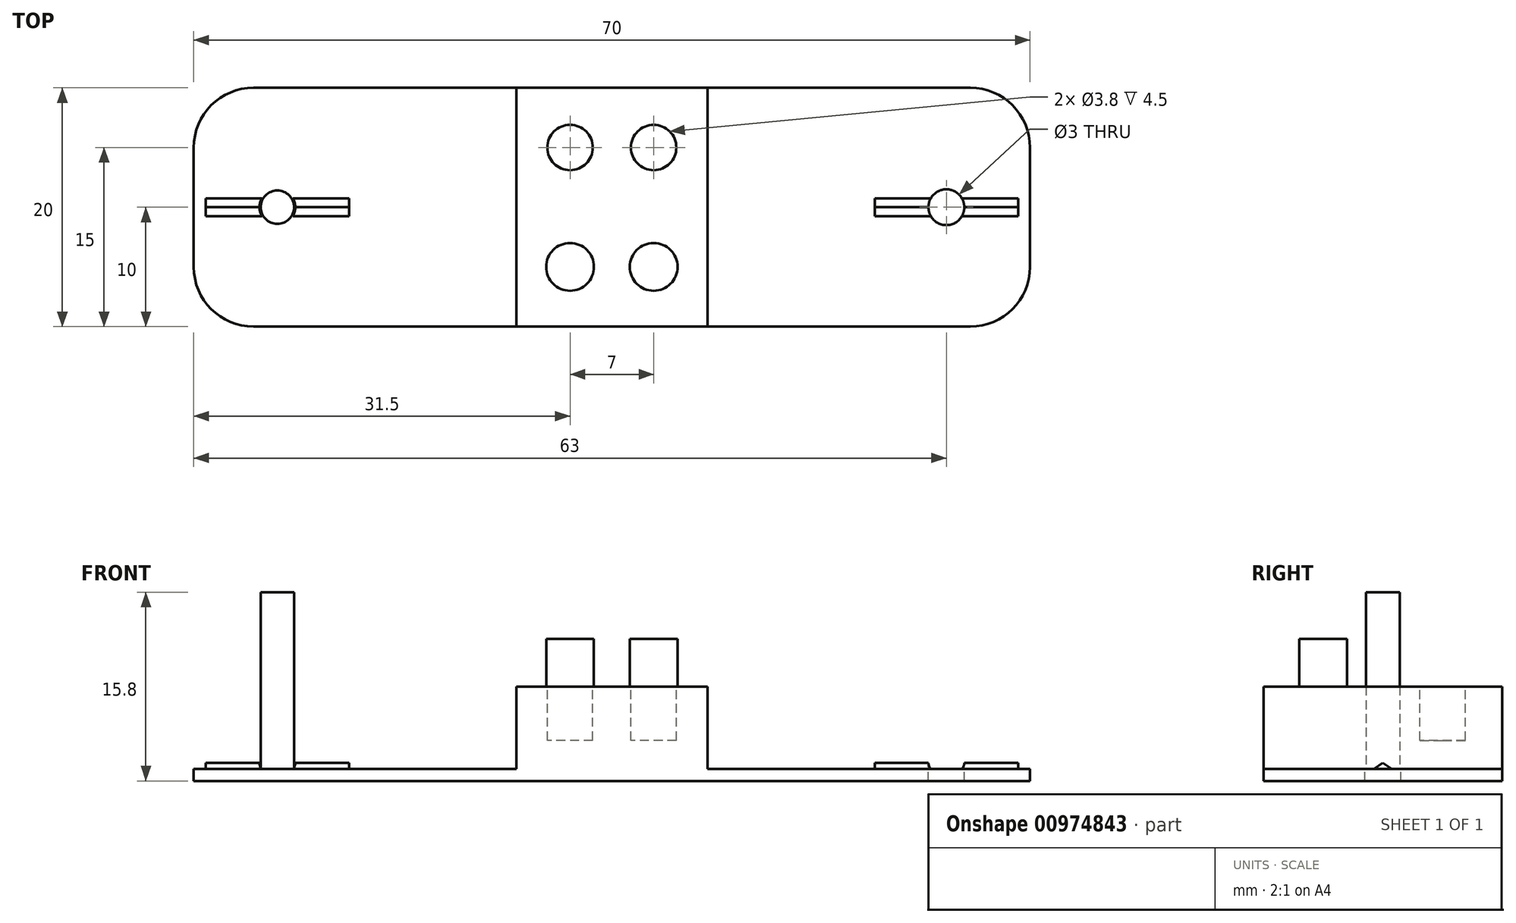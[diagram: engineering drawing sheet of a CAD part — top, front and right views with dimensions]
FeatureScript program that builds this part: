
annotation { "Feature Type Name" : "Feature", "Feature Type Description" : "" }
export const myFeature = defineFeature(function(context is Context, id is Id, definition is map)
    precondition{}
    {
        {
            var Q0;
            Q0=qCreatedBy(makeId("Top.planeOp"),FACE);
            var sketch = newSketch(context, id + "F0", { "sketchPlane" : qUnion([Q0])});
            skLineSegment(sketch, "E0.bottom", {"start": v(35, 10) * mm, "end": v(-35, 10) * mm});
            skLineSegment(sketch, "E0.top", {"start": v(35, -10) * mm, "end": v(-35, -10) * mm});
            skLineSegment(sketch, "E0.left", {"start": v(35, 10) * mm, "end": v(35, -10) * mm});
            skLineSegment(sketch, "E0.right", {"start": v(-35, 10) * mm, "end": v(-35, -10) * mm});
            skSolve(sketch);
        }
        {
            var Q0;
            Q0=qSketchRegion(id+"F0",true);
            extrude(context, id + "F1", {"entities" : qUnion([Q0]), "depth" : 1 * mm, "offsetDistance" : 25 * mm});
        }
        {
            var Q0;
            Q0=makeQuery(id+"F1.opExtrude","CAP_FACE",FACE,{"disambiguationData":[OSD([sQuery(id+"F0.wireOp",EDGE,"E0.bottom"),sQuery(id+"F0.wireOp",EDGE,"E0.top"),sQuery(id+"F0.wireOp",EDGE,"E0.left"),sQuery(id+"F0.wireOp",EDGE,"E0.right")])],"isStart":false});
            var sketch = newSketch(context, id + "F2", { "sketchPlane" : qUnion([Q0])});
            skCircle(sketch, "E1", {"center": v(-28, 0) * mm, "radius": 1.5 * mm});
            skPoint(sketch, "E1.centerSnap0", {"position": v(-35, 0) * mm});
            skCircle(sketch, "E2", {"center": v(28, 0) * mm, "radius": 1.5 * mm});
            skPoint(sketch, "E2.centerSnap0", {"position": v(35, 0) * mm});
            skSolve(sketch);
        }
        {
            var Q0;
            Q0=sQuery(id+"F2.wireOp",VERTEX,"E1.center");
            var Q1;
            Q1=sQuery(id+"F2.wireOp",VERTEX,"E2.center");
            var Q2;
            Q2=makeQuery(id+"F1.opExtrude","SWEPT_BODY",BODY,{"disambiguationData":[OSD([sQuery(id+"F0.wireOp",EDGE,"E0.bottom"),sQuery(id+"F0.wireOp",EDGE,"E0.top"),sQuery(id+"F0.wireOp",EDGE,"E0.left"),sQuery(id+"F0.wireOp",EDGE,"E0.right")])]});
            hole(context, id + "F3", {"style" : HoleStyle.SIMPLE, "endStyle" : HoleEndStyle.THROUGH, "holeDiameter" : 3 * mm, "majorDiameter" : 5 * mm, "isTappedThrough" : true, "tappedDepth" : 12 * mm, "tapClearance" : 3, "locations" : qUnion([Q0, Q1]), "scope" : qUnion([Q2])});
        }
        {
            var Q0;
            Q0=makeQuery(id+"F1.opExtrude","SWEPT_EDGE",EDGE,{"disambiguationData":[OSD([sQuery(id+"F0.wireOp",EDGE,"E0.bottom"),sQuery(id+"F0.wireOp",EDGE,"E0.right")])]});
            var Q1;
            Q1=makeQuery(id+"F1.opExtrude","SWEPT_EDGE",EDGE,{"disambiguationData":[OSD([sQuery(id+"F0.wireOp",EDGE,"E0.top"),sQuery(id+"F0.wireOp",EDGE,"E0.right")])]});
            var Q2;
            Q2=makeQuery(id+"F1.opExtrude","SWEPT_EDGE",EDGE,{"disambiguationData":[OSD([sQuery(id+"F0.wireOp",EDGE,"E0.bottom"),sQuery(id+"F0.wireOp",EDGE,"E0.left")])]});
            var Q3;
            Q3=makeQuery(id+"F1.opExtrude","SWEPT_EDGE",EDGE,{"disambiguationData":[OSD([sQuery(id+"F0.wireOp",EDGE,"E0.top"),sQuery(id+"F0.wireOp",EDGE,"E0.left")])]});
            fillet(context, id + "F4", {"entities" : qUnion([Q0, Q1, Q2, Q3]), "radius" : 5 * mm, "tangentPropagation" : true, "allowEdgeOverflow" : false});
        }
        {
            var Q0;
            Q0=makeQuery(id+"F1.opExtrude","CAP_FACE",FACE,{"disambiguationData":[OSD([sQuery(id+"F0.wireOp",EDGE,"E0.bottom"),sQuery(id+"F0.wireOp",EDGE,"E0.top"),sQuery(id+"F0.wireOp",EDGE,"E0.left"),sQuery(id+"F0.wireOp",EDGE,"E0.right")])],"isStart":false});
            var sketch = newSketch(context, id + "F5", { "sketchPlane" : qUnion([Q0])});
            skLineSegment(sketch, "E3", {"start": v(-34, 0.75) * mm, "end": v(-29.3, 0.75) * mm});
            skLineSegment(sketch, "E4", {"start": v(-22, 0.75) * mm, "end": v(-22, -0.75) * mm});
            skLineSegment(sketch, "E5", {"start": v(-22, -0.75) * mm, "end": v(-26.7, -0.75) * mm});
            skLineSegment(sketch, "E6", {"start": v(-34, -0.75) * mm, "end": v(-34, 0.75) * mm});
            skArc(sketch, "E7", {"start": v(-29.3, 0.75) * mm, "mid": v(-29.5, 0) * mm, "end": v(-29.3, -0.75) * mm});
            skLineSegment(sketch, "E8.trimOffspring", {"start": v(-26.7, 0.75) * mm, "end": v(-22, 0.75) * mm});
            skLineSegment(sketch, "E9.trimOffspring", {"start": v(-29.3, -0.75) * mm, "end": v(-34, -0.75) * mm});
            skArc(sketch, "E10.trimOffspring", {"start": v(-26.7, -0.75) * mm, "mid": v(-26.5, 0) * mm, "end": v(-26.7, 0.75) * mm});
            skSolve(sketch);
        }
        {
            var Q0;
            Q0=makeQuery(id+"F1.opExtrude","CAP_FACE",FACE,{"disambiguationData":[OSD([sQuery(id+"F0.wireOp",EDGE,"E0.bottom"),sQuery(id+"F0.wireOp",EDGE,"E0.top"),sQuery(id+"F0.wireOp",EDGE,"E0.left"),sQuery(id+"F0.wireOp",EDGE,"E0.right")])],"isStart":false});
            var sketch = newSketch(context, id + "F6", { "sketchPlane" : qUnion([Q0])});
            skLineSegment(sketch, "E11", {"start": v(22, 0.75) * mm, "end": v(26.7, 0.75) * mm});
            skLineSegment(sketch, "E12", {"start": v(34, 0.75) * mm, "end": v(34, -0.75) * mm});
            skLineSegment(sketch, "E13", {"start": v(34, -0.75) * mm, "end": v(29.3, -0.75) * mm});
            skLineSegment(sketch, "E14", {"start": v(22, -0.75) * mm, "end": v(22, 0.75) * mm});
            skArc(sketch, "E15", {"start": v(26.7, 0.75) * mm, "mid": v(26.5, 0) * mm, "end": v(26.7, -0.75) * mm});
            skLineSegment(sketch, "E16.trimOffspring", {"start": v(29.3, 0.75) * mm, "end": v(34, 0.75) * mm});
            skLineSegment(sketch, "E17.trimOffspring", {"start": v(26.7, -0.75) * mm, "end": v(22, -0.75) * mm});
            skArc(sketch, "E18.trimOffspring", {"start": v(29.3, -0.75) * mm, "mid": v(29.5, 0) * mm, "end": v(29.3, 0.75) * mm});
            skSolve(sketch);
        }
        {
            var Q0;
            Q0=makeQuery(id+"F5.imprint","IMPRINT",FACE,{"disambiguationData":[TD([[makeQuery(id+"F5.imprint","IMPRINT",EDGE,{"derivedFrom":sQuery(id+"F5.wireOp",EDGE,"E3")}),-1.0]])]});
            var Q1;
            Q1=makeQuery(id+"F5.imprint","IMPRINT",FACE,{"disambiguationData":[TD([[makeQuery(id+"F5.imprint","IMPRINT",EDGE,{"derivedFrom":sQuery(id+"F5.wireOp",EDGE,"E4")}),-1.0]])]});
            var Q2;
            Q2=makeQuery(id+"F6.imprint","IMPRINT",FACE,{"disambiguationData":[TD([[makeQuery(id+"F6.imprint","IMPRINT",EDGE,{"derivedFrom":sQuery(id+"F6.wireOp",EDGE,"E11")}),-1.0]])]});
            var Q3;
            Q3=makeQuery(id+"F6.imprint","IMPRINT",FACE,{"disambiguationData":[TD([[makeQuery(id+"F6.imprint","IMPRINT",EDGE,{"derivedFrom":sQuery(id+"F6.wireOp",EDGE,"E12")}),-1.0]])]});
            extrude(context, id + "F7", {"entities" : qUnion([Q0, Q1, Q2, Q3]), "operationType" : NewBodyOperationType.ADD, "depth" : 0.5 * mm, "offsetDistance" : 25 * mm});
        }
        {
            var Q0;
            Q0=makeQuery(id+"F7.opExtrude","SWEPT_FACE",FACE,{"disambiguationData":[OSD([sQuery(id+"F5.wireOp",EDGE,"E6")])]});
            var sketch = newSketch(context, id + "F8", { "sketchPlane" : qUnion([Q0])});
            skLineSegment(sketch, "E19", {"start": v(-0.75, 1) * mm, "end": v(0, 1.5) * mm});
            skLineSegment(sketch, "E20", {"start": v(0, 1.5) * mm, "end": v(0.75, 1) * mm});
            skLineSegment(sketch, "E21", {"start": v(0.75, 1) * mm, "end": v(-0.75, 1) * mm});
            skSolve(sketch);
        }
        {
            var Q0;
            {var subQ0=sQuery(id+"F8.wireOp",EDGE,"E19");Q0=makeQuery(id+"F8.imprint","IMPRINT",FACE,{"disambiguationData":[TD([[makeQuery(id+"F8.imprint","IMPRINT",EDGE,{"derivedFrom":subQ0}),1.0]])]});}
            var Q1;
            {var subQ0=sQuery(id+"F8.wireOp",EDGE,"E20");Q1=makeQuery(id+"F8.imprint","IMPRINT",FACE,{"disambiguationData":[TD([[makeQuery(id+"F8.imprint","IMPRINT",EDGE,{"derivedFrom":subQ0}),1.0]])]});}
            extrude(context, id + "F9", {"entities" : qUnion([Q0, Q1]), "operationType" : NewBodyOperationType.REMOVE, "endBound" : BoundingType.THROUGH_ALL, "oppositeDirection" : true, "depth" : 25 * mm, "offsetDistance" : 25 * mm});
        }
        {
            var Q0;
            Q0=makeQuery(id+"F1.opExtrude","CAP_FACE",FACE,{"disambiguationData":[OSD([sQuery(id+"F0.wireOp",EDGE,"E0.bottom"),sQuery(id+"F0.wireOp",EDGE,"E0.top"),sQuery(id+"F0.wireOp",EDGE,"E0.left"),sQuery(id+"F0.wireOp",EDGE,"E0.right")])],"isStart":false});
            var sketch = newSketch(context, id + "F10", { "sketchPlane" : qUnion([Q0])});
            skLineSegment(sketch, "E22.bottom", {"start": v(-8, -10) * mm, "end": v(8, -10) * mm});
            skLineSegment(sketch, "E22.top", {"start": v(-8, 10) * mm, "end": v(8, 10) * mm});
            skLineSegment(sketch, "E22.left", {"start": v(-8, -10) * mm, "end": v(-8, 10) * mm});
            skLineSegment(sketch, "E22.right", {"start": v(8, -10) * mm, "end": v(8, 10) * mm});
            skPoint(sketch, "E22.middle", {"position": v(0, 0) * mm});
            skSolve(sketch);
        }
        {
            var Q0;
            Q0=makeQuery(id+"F10.imprint","IMPRINT",FACE,{"disambiguationData":[TD([[makeQuery(id+"F10.imprint","IMPRINT",EDGE,{"derivedFrom":sQuery(id+"F10.wireOp",EDGE,"E22.bottom")}),-1.0]])]});
            extrude(context, id + "F11", {"entities" : qUnion([Q0]), "operationType" : NewBodyOperationType.ADD, "depth" : 6.9 * mm, "offsetDistance" : 25 * mm});
        }
        {
            var Q0;
            Q0=makeQuery(id+"F11.opExtrude","CAP_FACE",FACE,{"disambiguationData":[OSD([sQuery(id+"F10.wireOp",EDGE,"E22.bottom"),sQuery(id+"F10.wireOp",EDGE,"E22.top"),sQuery(id+"F10.wireOp",EDGE,"E22.left"),sQuery(id+"F10.wireOp",EDGE,"E22.right")])],"isStart":false});
            var sketch = newSketch(context, id + "F12", { "sketchPlane" : qUnion([Q0])});
            skCircle(sketch, "E23", {"center": v(-3.5, 5) * mm, "radius": 1.9 * mm});
            skCircle(sketch, "E24", {"center": v(3.5, 5) * mm, "radius": 1.9 * mm});
            skCircle(sketch, "E25", {"center": v(-3.5, -5) * mm, "radius": 2 * mm});
            skCircle(sketch, "E26", {"center": v(3.5, -5) * mm, "radius": 2 * mm});
            skSolve(sketch);
        }
        {
            var Q0;
            Q0=makeQuery(id+"F12.imprint","IMPRINT",FACE,{"disambiguationData":[TD([[makeQuery(id+"F12.imprint","IMPRINT",EDGE,{"derivedFrom":sQuery(id+"F12.wireOp",EDGE,"E23")}),1.0]])]});
            var Q1;
            Q1=makeQuery(id+"F12.imprint","IMPRINT",FACE,{"disambiguationData":[TD([[makeQuery(id+"F12.imprint","IMPRINT",EDGE,{"derivedFrom":sQuery(id+"F12.wireOp",EDGE,"E24")}),1.0]])]});
            extrude(context, id + "F13", {"entities" : qUnion([Q0, Q1]), "operationType" : NewBodyOperationType.REMOVE, "oppositeDirection" : true, "depth" : 4.5 * mm, "offsetDistance" : 25 * mm});
        }
        {
            var Q0;
            Q0=makeQuery(id+"F11.opExtrude","CAP_FACE",FACE,{"disambiguationData":[OSD([sQuery(id+"F10.wireOp",EDGE,"E22.bottom"),sQuery(id+"F10.wireOp",EDGE,"E22.top"),sQuery(id+"F10.wireOp",EDGE,"E22.left"),sQuery(id+"F10.wireOp",EDGE,"E22.right")])],"isStart":false});
            var sketch = newSketch(context, id + "F14", { "sketchPlane" : qUnion([Q0])});
            skCircle(sketch, "E27", {"center": v(-3.5, 5) * mm, "radius": 1.95 * mm});
            skCircle(sketch, "E28", {"center": v(3.5, 5) * mm, "radius": 1.95 * mm});
            skCircle(sketch, "E29", {"center": v(-3.5, -5) * mm, "radius": 2 * mm});
            skCircle(sketch, "E30", {"center": v(3.5, -5) * mm, "radius": 2 * mm});
            skSolve(sketch);
        }
        {
            var Q0;
            Q0=makeQuery(id+"F14.imprint","IMPRINT",FACE,{"disambiguationData":[TD([[makeQuery(id+"F14.imprint","IMPRINT",EDGE,{"derivedFrom":sQuery(id+"F14.wireOp",EDGE,"E29")}),1.0]])]});
            var Q1;
            Q1=makeQuery(id+"F14.imprint","IMPRINT",FACE,{"disambiguationData":[TD([[makeQuery(id+"F14.imprint","IMPRINT",EDGE,{"derivedFrom":sQuery(id+"F14.wireOp",EDGE,"E30")}),1.0]])]});
            extrude(context, id + "F15", {"entities" : qUnion([Q0, Q1]), "operationType" : NewBodyOperationType.ADD, "depth" : 4 * mm, "offsetDistance" : 25 * mm});
        }
        {
            var Q0;
            {var subQ2=sQuery(id+"F0.wireOp",EDGE,"E0.right");var subQ3=sQuery(id+"F0.wireOp",EDGE,"E0.top");var subQ5=sQuery(id+"F0.wireOp",EDGE,"E0.bottom");var subQ9=makeQuery(id+"F1.opExtrude","CAP_FACE",FACE,{"disambiguationData":[OSD([subQ5,subQ3,sQuery(id+"F0.wireOp",EDGE,"E0.left"),subQ2])],"isStart":false});Q0=makeQuery(id+"F11.boolean.opBoolean","SPLIT",FACE,{"disambiguationData":[TD([makeQuery(id+"F1.opExtrude","SWEPT_FACE",FACE,{"disambiguationData":[OSD([subQ2])]})])],"derivedFrom":subQ9});}
            var sketch = newSketch(context, id + "F16", { "sketchPlane" : qUnion([Q0])});
            skCircle(sketch, "E31", {"center": v(-28, 0) * mm, "radius": 1.5 * mm});
            skSolve(sketch);
        }
        {
            var Q0;
            Q0=qSketchRegion(id+"F16",true);
            extrude(context, id + "F17", {"entities" : qUnion([Q0]), "operationType" : NewBodyOperationType.ADD, "oppositeDirection" : true, "depth" : 1 * mm, "offsetDistance" : 25 * mm});
        }
        {
            var Q0;
            {var subQ2=sQuery(id+"F0.wireOp",EDGE,"E0.right");var subQ3=sQuery(id+"F0.wireOp",EDGE,"E0.top");var subQ5=sQuery(id+"F0.wireOp",EDGE,"E0.bottom");var subQ9=makeQuery(id+"F1.opExtrude","CAP_FACE",FACE,{"disambiguationData":[OSD([subQ5,subQ3,sQuery(id+"F0.wireOp",EDGE,"E0.left"),subQ2])],"isStart":false});Q0=makeQuery(id+"F17.boolean.opBoolean","MERGE",FACE,{"derivedFrom":[makeQuery(id+"F11.boolean.opBoolean","SPLIT",FACE,{"disambiguationData":[TD([makeQuery(id+"F1.opExtrude","SWEPT_FACE",FACE,{"disambiguationData":[OSD([subQ2])]})])],"derivedFrom":subQ9}),makeQuery(id+"F17.opExtrude","CAP_FACE",FACE,{"disambiguationData":[OSD([sQuery(id+"F16.wireOp",EDGE,"E31")])],"isStart":true})]});}
            var sketch = newSketch(context, id + "F18", { "sketchPlane" : qUnion([Q0])});
            skCircle(sketch, "E32", {"center": v(-28, 0) * mm, "radius": 1.4 * mm});
            skSolve(sketch);
        }
        {
            var Q0;
            Q0=qSketchRegion(id+"F18",true);
            extrude(context, id + "F19", {"entities" : qUnion([Q0]), "operationType" : NewBodyOperationType.ADD, "depth" : 14.8 * mm, "offsetDistance" : 25 * mm});
        }
    });
